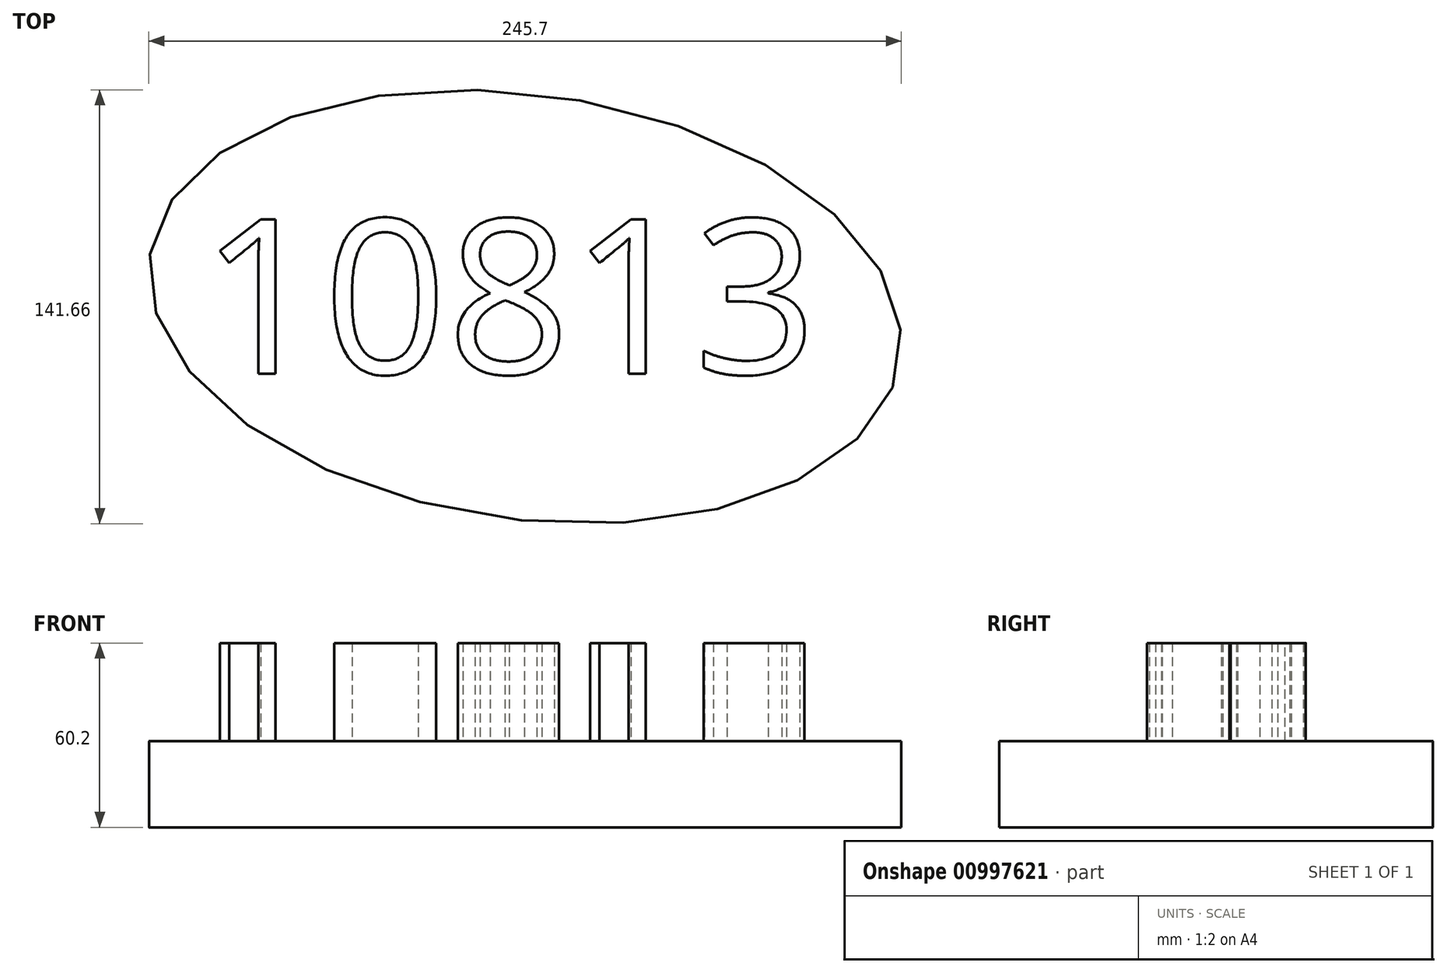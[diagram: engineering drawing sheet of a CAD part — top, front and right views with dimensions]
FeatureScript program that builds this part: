
annotation { "Feature Type Name" : "Feature", "Feature Type Description" : "" }
export const myFeature = defineFeature(function(context is Context, id is Id, definition is map)
    precondition{}
    {
        {
            var Q0;
            Q0=qCreatedBy(makeId("Top.planeOp"),FACE);
            var sketch = newSketch(context, id + "F0", { "sketchPlane" : qUnion([Q0])});
            skEllipse(sketch, "E0", {"center": v(0, 0) * mm, "majorRadius": 123.65 * mm, "minorRadius": 69.41 * mm, "majorAxis": v(-1, 0.14)});
            skSolve(sketch);
        }
        {
            var Q0;
            Q0=makeQuery(id+"F0.imprint","IMPRINT",FACE,{"disambiguationData":[TD([[makeQuery(id+"F0.imprint","IMPRINT",EDGE,{"derivedFrom":sQuery(id+"F0.wireOp",EDGE,"E0")}),1.0]])]});
            extrude(context, id + "F1", {"entities" : qUnion([Q0]), "depth" : 28.2 * mm, "offsetDistance" : 25.4 * mm});
        }
        {
            var Q0;
            Q0=makeQuery(id+"F1.opExtrude","CAP_FACE",FACE,{"disambiguationData":[OSD([sQuery(id+"F0.wireOp",EDGE,"E0")])],"isStart":false});
            var sketch = newSketch(context, id + "F2", { "sketchPlane" : qUnion([Q0])});
            skText(sketch, "E1", { "text": "10813", "fontName": "OpenSans-Regular.ttf"});
            const initialGuessF2  = {"E1": [-0.10614, -0.02183, 1, 0, 0.05076]};
            skSetInitialGuess(sketch, initialGuessF2);
            skSolve(sketch);
        }
        {
            var Q0;
            Q0 = qSketchRegion(id + "F2", true);
            extrude(context, id + "F3", {"entities" : qUnion([Q0]), "operationType" : NewBodyOperationType.ADD, "depth" : 32 * mm, "offsetDistance" : 25.4 * mm});
        }
    });
